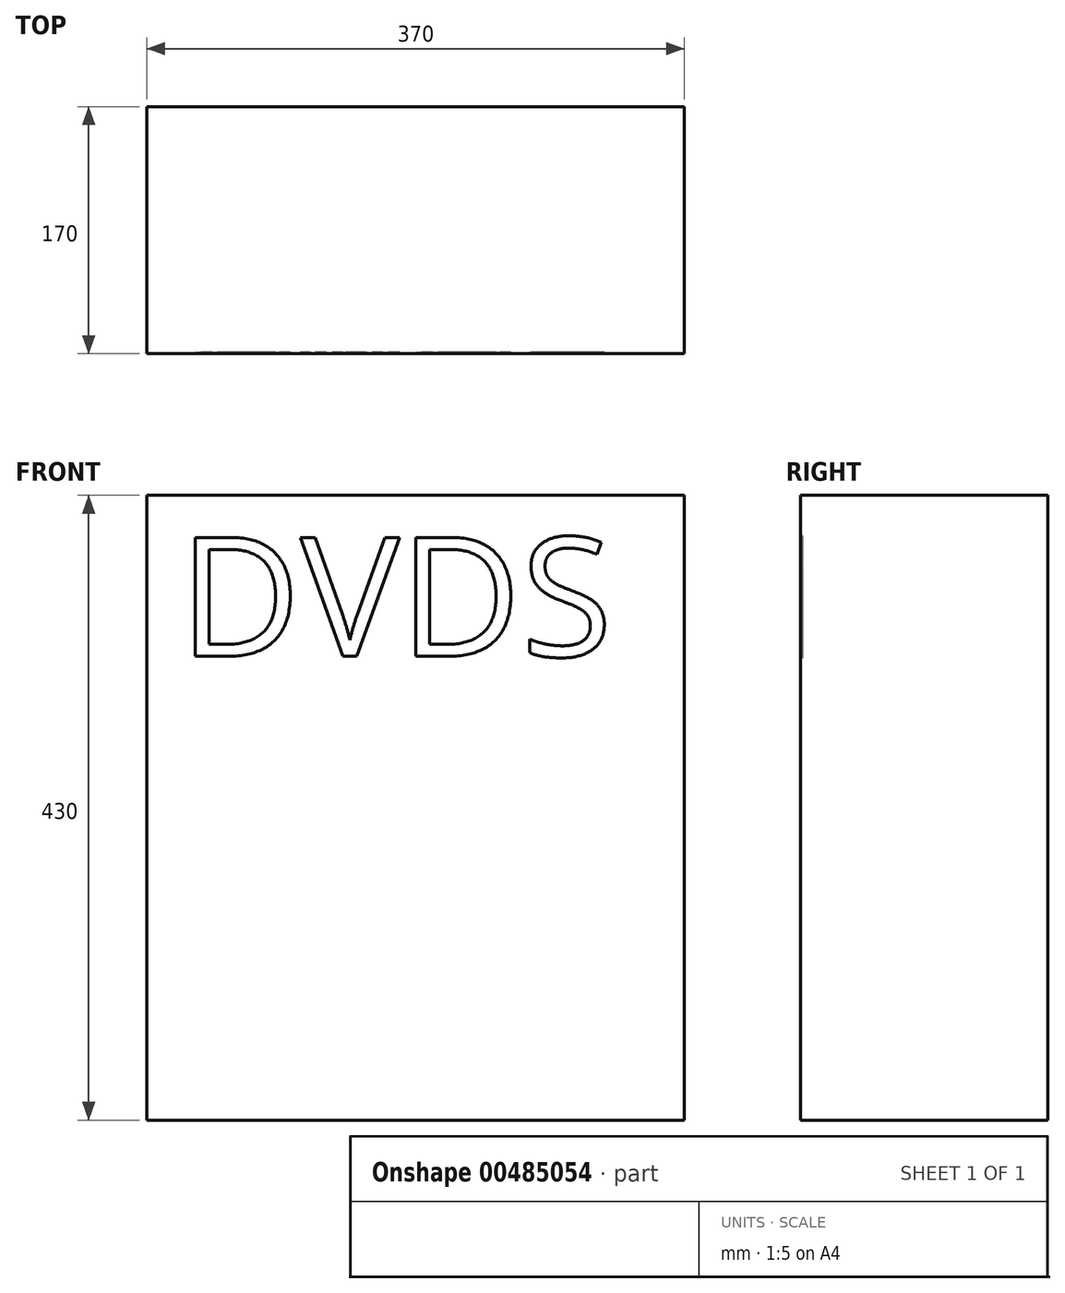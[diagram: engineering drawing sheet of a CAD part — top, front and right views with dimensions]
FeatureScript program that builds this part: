
annotation { "Feature Type Name" : "Feature", "Feature Type Description" : "" }
export const myFeature = defineFeature(function(context is Context, id is Id, definition is map)
    precondition{}
    {
        {
            var Q0;
            Q0=qCreatedBy(makeId("Top.planeOp"),FACE);
            var sketch = newSketch(context, id + "F0", { "sketchPlane" : qUnion([Q0])});
            skLineSegment(sketch, "E0.bottom", {"start": v(185, -85) * mm, "end": v(-185, -85) * mm});
            skLineSegment(sketch, "E0.top", {"start": v(185, 85) * mm, "end": v(-185, 85) * mm});
            skLineSegment(sketch, "E0.left", {"start": v(185, -85) * mm, "end": v(185, 85) * mm});
            skLineSegment(sketch, "E0.right", {"start": v(-185, -85) * mm, "end": v(-185, 85) * mm});
            skPoint(sketch, "E0.middle", {"position": v(0, 0) * mm});
            skSolve(sketch);
        }
        {
            var Q0;
            Q0=makeQuery(id+"F0.imprint","IMPRINT",FACE,{"disambiguationData":[TD([[makeQuery(id+"F0.imprint","IMPRINT",EDGE,{"derivedFrom":sQuery(id+"F0.wireOp",EDGE,"E0.bottom")}),-1.0]])]});
            extrude(context, id + "F1", {"entities" : qUnion([Q0]), "depth" : 430 * mm});
        }
        {
            var Q0;
            Q0=makeQuery(id+"F1.opExtrude","SWEPT_FACE",FACE,{"disambiguationData":[OSD([sQuery(id+"F0.wireOp",EDGE,"E0.bottom")])]});
            var sketch = newSketch(context, id + "F2", { "sketchPlane" : qUnion([Q0])});
            skText(sketch, "E1", { "text": "DVDS", "fontName": "OpenSans-Regular.ttf"});
            const initialGuessF2  = {"E1": [-0.16284, 0.3192, 1, 0, 0.0825]};
            skSetInitialGuess(sketch, initialGuessF2);
            skSolve(sketch);
        }
        {
            var Q0;
            Q0 = qSketchRegion(id + "F2", true);
            extrude(context, id + "F3", {"entities" : qUnion([Q0]), "operationType" : NewBodyOperationType.REMOVE, "oppositeDirection" : true, "depth" : 1 * mm});
        }
    });
